# Revit family: QF_BPRO_RWRA 582_572930
name_source: partatom
category: Sonderausstattung
revit_build: Autodesk Revit 2018 (Build: 20190510_1515(x64)
units: mm (PartAtom-declared; Revit-internal decimal feet)

## family parameters
Arbeitsebenenbasiert = Nein
Beim Laden mit Abzugskörper schneiden = Nein
Bemaßung runder Anschluss = Durchmesser verwenden
Gemeinsam genutzt = Nein
Immer vertikal = Ja
Raumberechnungspunkt = Nein
Teiletyp = Normal

## types (1)
- RWRA 852
    Abstand Einlagen = 73 mm
    Anzahl Schienen = 8
    Artikel Nummer = 572930
    Beschreibung = Regalwagen aus rostfreiem Edelstahl
Auflagenabstand: 16 Paar 73 mm
Kapazität: 16 GN 1/1 oder  32 GN 1/2
Tragfähigkeit: 180 kg
Wandabweiser aus Kunststoff (Polyamid) an allen vier Ecken
    Beschreibung durch Hersteller analog Leistungsverzeichniskurztext = Abmessungen

Länge:			820 mm
Breite:			613 mm
Höhe:			845 mm

Lichtes Maß:
Abstand der Auflagenschienen:	  73 mm


Ausführung

Der zweiteilige Regalwagen besteht aus CNS 18/10, Werkstoff-Nr. 1.4301. Zwischen stabilem Vierkantrohr mit 25 x 25 mm befinden sich eingeschweißte U-Profil-Führungsschienen. Diese sind mit einer Kippsicherung sowie einer beidseitigen Durchschubsicherung für GN 1/1, 2/3, 1/3 und 2/8 versehen. Der Regalwagen ist mit einer glatten Arbeitsplatte (748 x 542 mm)  ausgestattet die 4-seitig abgekantet ist. 

Der Regalwagen ist fahrbar mittels rostfreien Kunststoffrollen gemäß DIN 18867, Teil 8 (4 Lenkrollen, davon 2 mit Feststeller, Rollendurchmesser 125 mm). Wandabweiser aus Kunststoff (Polyamid) an allen vier Ecken schützen vor Beschädigung.


Zubehör/ Optionen

•	CNS-Verkleidung, 2- oder 3-seitig
•	Transportsicherungsbügel, beidseitig


Technische Daten

Werkstoff:	Chromnickelstahl 18/10,
		Polyamid (PA)
Materialstärke VK-Rohr:	1,5 mm
Materialstärke
Auflageschienen:		1,2 mm
Gewicht:		                        21 kg
Tragfähigkeit je Wagen:	180 kg
Anzahl Auflagenpaare:	16 (2 x 8)
Kapazität:		16 x GN 1/1 oder 32 x GN 1/2


Besonderheit

•	U-Profil-Führungsschienen mit Kipp- und beidseitiger Durchschubsicherung 
•	2-teilige Ausführung mit Arbeitsplatte
•	Zum Unterfahren in offene Arbeitstische


Fabrikat

Hersteller:	B.PRO
Typ:                                      RWRA 852
Best.Nr.		572 930
    Beschreibung durch Hersteller analog Leistungsverzeichnislangtext = Abmessungen

Länge:			820 mm
Breite:			613 mm
Höhe:			845 mm

Lichtes Maß:
Abstand der Auflagenschienen:	  73 mm


Ausführung

Der zweiteilige Regalwagen besteht aus CNS 18/10, Werkstoff-Nr. 1.4301. Zwischen stabilem Vierkantrohr mit 25 x 25 mm befinden sich eingeschweißte U-Profil-Führungsschienen. Diese sind mit einer Kippsicherung sowie einer beidseitigen Durchschubsicherung für GN 1/1, 2/3, 1/3 und 2/8 versehen. Der Regalwagen ist mit einer glatten Arbeitsplatte (748 x 542 mm)  ausgestattet die 4-seitig abgekantet ist. 

Der Regalwagen ist fahrbar mittels rostfreien Kunststoffrollen gemäß DIN 18867, Teil 8 (4 Lenkrollen, davon 2 mit Feststeller, Rollendurchmesser 125 mm). Wandabweiser aus Kunststoff (Polyamid) an allen vier Ecken schützen vor Beschädigung.


Zubehör/ Optionen

•	CNS-Verkleidung, 2- oder 3-seitig
•	Transportsicherungsbügel, beidseitig


Technische Daten

Werkstoff:	Chromnickelstahl 18/10,
		Polyamid (PA)
Materialstärke VK-Rohr:	1,5 mm
Materialstärke
Auflageschienen:		1,2 mm
Gewicht:		                        21 kg
Tragfähigkeit je Wagen:	180 kg
Anzahl Auflagenpaare:	16 (2 x 8)
Kapazität:		16 x GN 1/1 oder 32 x GN 1/2


Besonderheit

•	U-Profil-Führungsschienen mit Kipp- und beidseitiger Durchschubsicherung 
•	2-teilige Ausführung mit Arbeitsplatte
•	Zum Unterfahren in offene Arbeitstische


Fabrikat

Hersteller:	B.PRO
Typ:                                      RWRA 852
Best.Nr.		572 930
    Gerätegewicht Netto = 21.00 kg
    Großküchengerätezuordnung = Ja
    Hersteller = B.PRO GmbH
    Höhe = 845 mm  [stored 2.77231 ft]
    Internetadresse Gerätehersteller = https://www.bpro-solutions.com
    Internetadresse für Ersatzteilliste = https://www.bpro-solutions.com
    Kosten = 1010.4 $
    Länge Gerätebreite = 820 mm
    Länge Korpus = 745 mm  [stored 2.44423 ft]
    Material = QF_Metal-Stainless-Steel_general
    Material_Stoßschutz = QF_Rubber-Black-Matt
    Modell = RWRA 852
    Sockelhöhe = 174 mm  [stored 0.570866 ft]
    Tiefe = 613 mm
    Tiefe Korpus = 538 mm  [stored 1.76509 ft]
    Typenkommentare = Regalwagen mit Arbeitsplatte, 2-teilig
    URL = https://www.bpro-solutions.com
    Versatz Einlage unten = 65 mm
    Zubehör = Nein

note: [stored X ft] marks values corroborated as IEEE doubles in the binary element streams (Revit-internal decimal feet)
